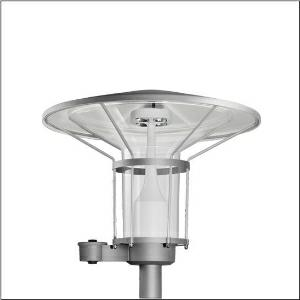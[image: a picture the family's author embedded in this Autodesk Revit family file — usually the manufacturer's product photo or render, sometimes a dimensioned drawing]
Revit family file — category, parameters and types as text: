
# Revit family: laterne_classic_iq___st1_2a_5xa5245eu14h000022_d57d
name_source: partatom
category: Lighting Fixtures
units: mm (PartAtom-declared; Revit-internal decimal feet)

## family parameters
Cut with Voids When Loaded = No
Host = Face
Light Source = No
Part Type = Normal
Room Calculation Point = No
Round Connector Dimension = Use Diameter
Shared = No

## types (1)
- --- (1 x LED, 1370 lm, 10.7 W, 3000K)
    Apparent Load = 11 VA
    CIE Flux Codes = 21 60 93 97 100
    Color Rendering = 70
    Color Temperature = 3000K
    Default Elevation = 1800 mm
    Description = Lantern Classic iQ, mast luminaire, Module 540 iQ-SR, primary light control with 3 zone facetted reflector, of plastic, silver coated, highly specular, structured, primary optical cover: cover, of PMMA, transparent, light distribution: ST1.2a, light emission: direct distribution, primary light characteristic: asymmetric, installation type: post-top, LED, High Power LED, rated luminous flux: 1.370lm, luminous efficacy: 128lm/W, light colour: 730, colour temperature: 3000K, control gear: iQ-Street Remote, D4i with power reduction, control: optimised constant luminous flux control (CLO 2.0), Desk-Remote (wireless, voltage-free reading and setting of iQ features in the workshop via application-optimized NFC function/RFID function), Light-Fading, Smart-Wire, Night-Set, Lumen-Switch, Temp-Guard, Auto-Match, Street-Remote, pre-setting: logarithmic dimming characteristic, with terminal, 6-pole, max. 2.5mm², mains connection: 230..240V, AC, 50/60Hz, connection cable pre-assembled, cable length: 5,5m, wiring characteristics: H07RN-F, start of lifetime: 11W, end of service life: 11W, reduction: 6W, luminaire housing, upper part, of glass-fibre reinforced polyester, coated, Siteco® metallic grey (DB 702S), diameter: 750mm, height: 596mm, spigot size: d x l = 76 x 70mm (post-top) | with reducer (optional accessory) 60 x 70mm, mounting height: 3..5m, post-top mast mounting element, of diecast aluminium, coated, Siteco® metallic grey (DB 702S), Module 540 iQ-SR, traffic white (RAL 9016), equipment: standard, Smart Interface below, protection rating (complete): IP65, insulation class (complete): insulation class II (safety insulation), certification: CE, ENEC, VDE, packaging unit: 1 piece

Light Distribution: ST1.2a
    Height = 596 mm
    Lamp = 1 x LED
    Lamp Light Flux = 1370 lm
    Lamp Power = 10.7 W
    Lamp count = 1
    Length = 750 mm
    Luminous efficacy = 128 lm/W
    Manufacturer = Siteco
    ModVariant = No
    Model = 5XA5245EU14H000022
    Number of Poles = 1
    OnlyDefault = Yes
    Power Factor = 1
    Product Name = Laterne Classic iQ | ST1.2a
    Product group = mast luminaire | pylon top
    ProductGroupID = 6100
    Protection Class = Protection class II
    Protection Degree = IP 65
    RLX_Detail_Level = 1
    RLX_Emergency_Light_Flux = 0 lm
    RLX_Emergency_Type = 0
    RLX_Emergency_Type_DB = No
    RlxData = <blob elided: 64041 chars, md5=e3f8ccc9>
    Socket = socket
    Standby Power = 0 W
    System Light Flux = 1370 lm
    System Power = 11 W
    Type Comments = factory setting: luminous flux: 100 % | dim-lin: 254 | 419 mA
    Type Image = l_1006522.jpg
    URL = http://relux.com
    VarID = @adj_086640
    Voltage = 0 V
    Weight = 0.00 kg
    Width = 0 mm  [stored 0 ft]

note: [stored X ft] marks values corroborated as IEEE doubles in the binary element streams (Revit-internal decimal feet)

## geometry (parser evidence)
native form markers: Blend x4, Sweep x7
no freeform markers — native parametric forms only
